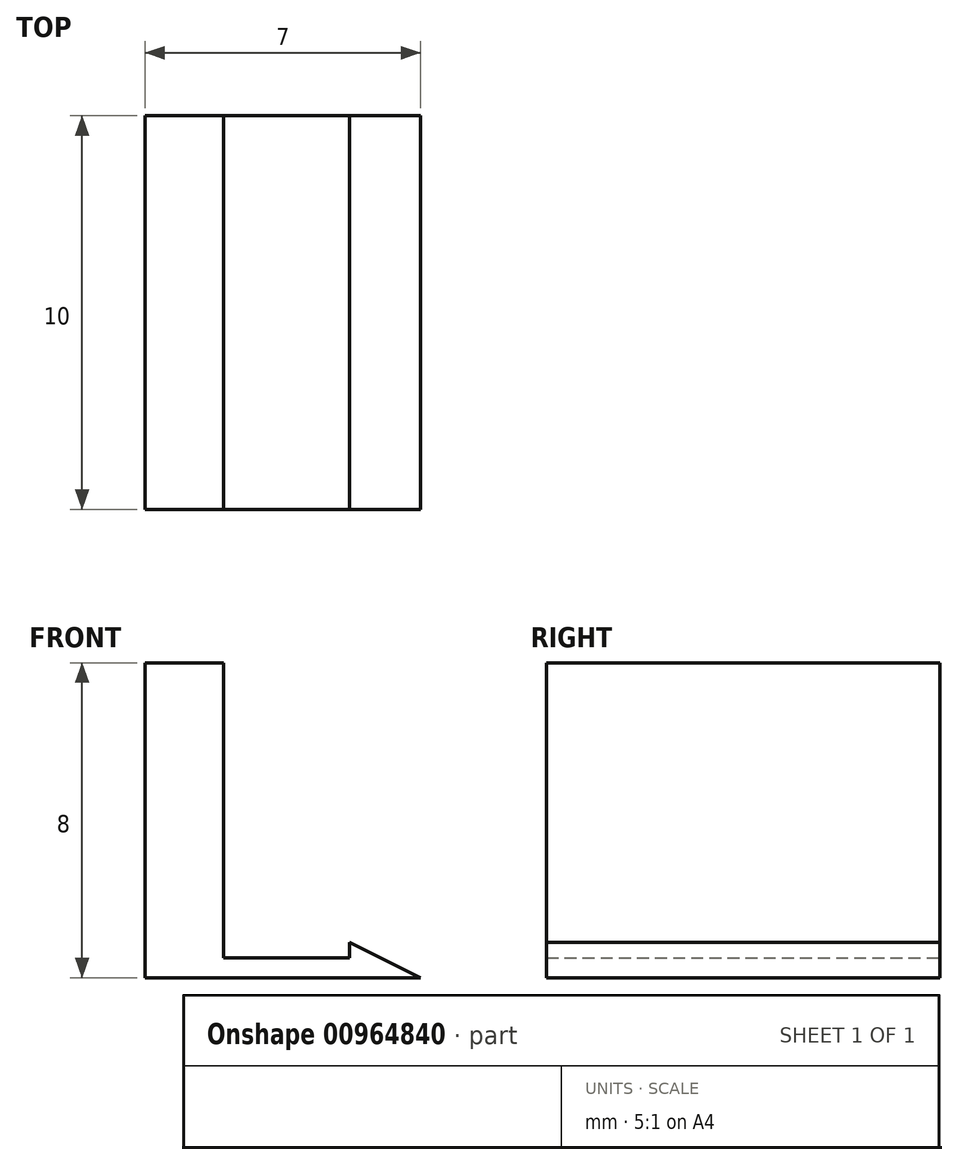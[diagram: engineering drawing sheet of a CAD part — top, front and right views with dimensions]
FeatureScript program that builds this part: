
annotation { "Feature Type Name" : "Feature", "Feature Type Description" : "" }
export const myFeature = defineFeature(function(context is Context, id is Id, definition is map)
    precondition{}
    {
        {
            var Q0;
            Q0=qCreatedBy(makeId("Front.planeOp"),FACE);
            var sketch = newSketch(context, id + "F0", { "sketchPlane" : qUnion([Q0])});
            skLineSegment(sketch, "E0", {"start": v(0, 0) * mm, "end": v(7, 0) * mm});
            skLineSegment(sketch, "E1", {"start": v(0, 0) * mm, "end": v(0, 2) * mm});
            skLineSegment(sketch, "E2", {"start": v(0, 2) * mm, "end": v(0, 8) * mm});
            skLineSegment(sketch, "E3", {"start": v(0, 8) * mm, "end": v(2, 8) * mm});
            skLineSegment(sketch, "E4", {"start": v(2, 8) * mm, "end": v(2, 0.5) * mm});
            skLineSegment(sketch, "E5", {"start": v(2, 0.5) * mm, "end": v(5.2, 0.5) * mm});
            skLineSegment(sketch, "E6", {"start": v(7, 0) * mm, "end": v(5.2, 0.9) * mm});
            skLineSegment(sketch, "E7", {"start": v(5.2, 0.5) * mm, "end": v(5.2, 0.9) * mm});
            skSolve(sketch);
        }
        {
            var Q0;
            Q0=makeQuery(id+"F0.imprint","IMPRINT",FACE,{"disambiguationData":[TD([[makeQuery(id+"F0.imprint","IMPRINT",EDGE,{"derivedFrom":sQuery(id+"F0.wireOp",EDGE,"E0")}),1.0]])]});
            extrude(context, id + "F1", {"entities" : qUnion([Q0]), "depth" : 10 * mm, "offsetDistance" : 25 * mm});
        }
    });
